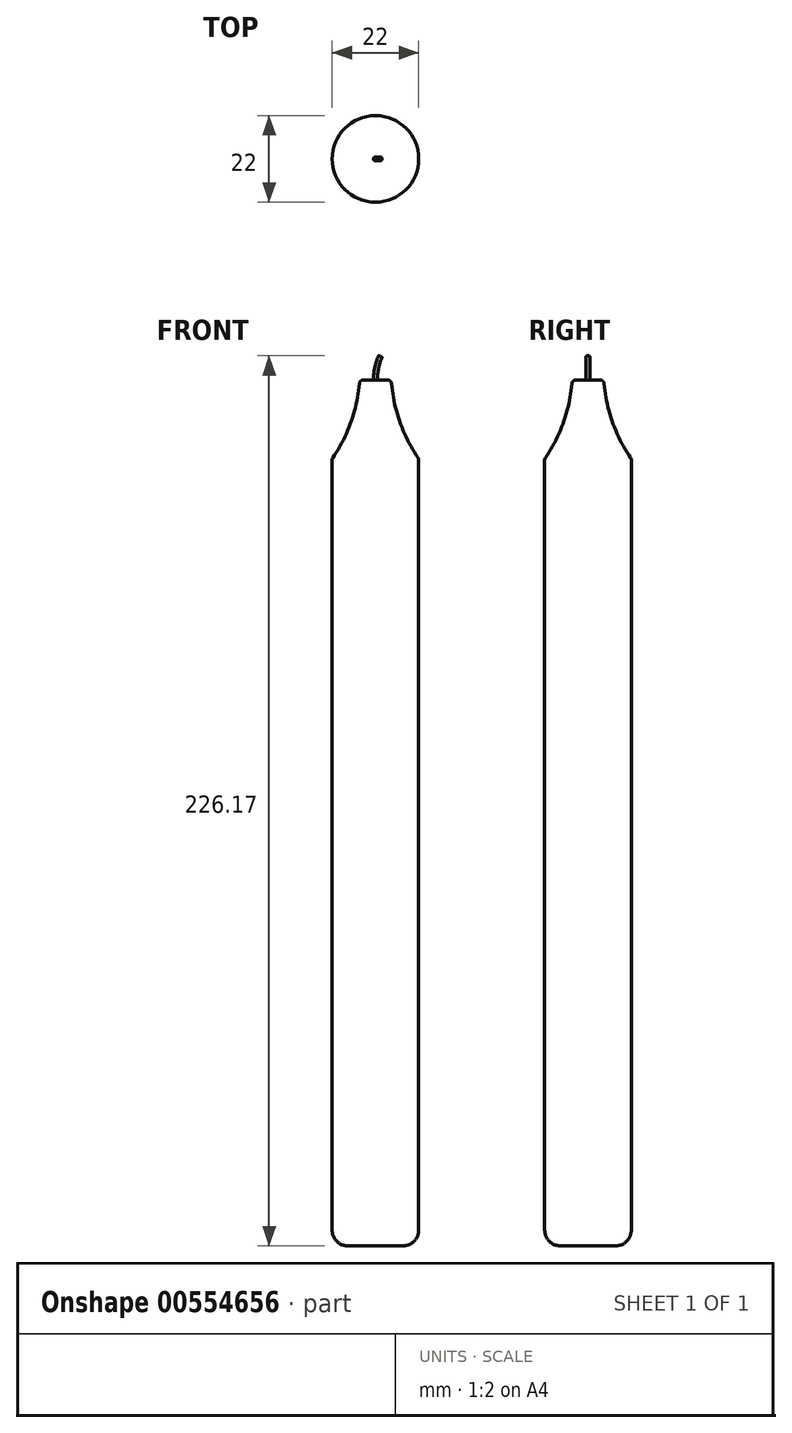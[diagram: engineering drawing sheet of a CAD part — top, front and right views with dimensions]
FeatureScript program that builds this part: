
annotation { "Feature Type Name" : "Feature", "Feature Type Description" : "" }
export const myFeature = defineFeature(function(context is Context, id is Id, definition is map)
    precondition{}
    {
        {
            var Q0;
            Q0=qCreatedBy(makeId("Front.planeOp"),FACE);
            var sketch = newSketch(context, id + "F0", { "sketchPlane" : qUnion([Q0])});
            skLineSegment(sketch, "E0", {"start": v(0, 0) * mm, "end": v(11, 0) * mm});
            skLineSegment(sketch, "E1", {"start": v(11, 0) * mm, "end": v(11, 200) * mm});
            skLineSegment(sketch, "E2", {"start": v(4, 220) * mm, "end": v(0, 220) * mm});
            skLineSegment(sketch, "E3", {"start": v(0, 220) * mm, "end": v(0, 0) * mm});
            skArc(sketch, "E4", {"start": v(4, 220) * mm, "mid": v(6.15, 209.53) * mm, "end": v(11, 200) * mm});
            skSolve(sketch);
        }
        {
            var Q0;
            Q0=makeQuery(id+"F0.imprint","IMPRINT",FACE,{"disambiguationData":[TD([[makeQuery(id+"F0.imprint","IMPRINT",EDGE,{"derivedFrom":sQuery(id+"F0.wireOp",EDGE,"E0")}),1.0]])]});
            var Q1;
            Q1=sQuery(id+"F0.wireOp",EDGE,"E3");
            revolve(context, id + "F1", {"entities" : qUnion([Q0]), "axis" : qUnion([Q1]), "revolveType" : RevolveType.FULL});
        }
        {
            var Q0;
            Q0=qCreatedBy(makeId("Front.planeOp"),FACE);
            var sketch = newSketch(context, id + "F2", { "sketchPlane" : qUnion([Q0])});
            skArc(sketch, "E5", {"start": v(1.25, 226) * mm, "mid": v(0.32, 223.06) * mm, "end": v(0, 220) * mm});
            skLineSegment(sketch, "E6", {"start": v(0, 220) * mm, "end": v(0, 0) * mm, "construction": true});
            skSolve(sketch);
        }
        {
            var Q0;
            Q0=makeQuery(id+"F1.opRevolve","SWEPT_FACE",FACE,{"disambiguationData":[OSD([sQuery(id+"F0.wireOp",EDGE,"E2")])]});
            var sketch = newSketch(context, id + "F3", { "sketchPlane" : qUnion([Q0])});
            skCircle(sketch, "E7", {"center": v(0, 0) * mm, "radius": 0.5 * mm});
            skSolve(sketch);
        }
        {
            var Q0;
            Q0=makeQuery(id+"F3.imprint","IMPRINT",FACE,{"disambiguationData":[TD([[makeQuery(id+"F3.imprint","IMPRINT",EDGE,{"derivedFrom":sQuery(id+"F3.wireOp",EDGE,"E7")}),1.0]])]});
            var Q1;
            Q1=sQuery(id+"F3.wireOp",EDGE,"E7");
            var Q2;
            Q2=sQuery(id+"F2.wireOp",EDGE,"E5");
            sweep(context, id + "F4", {"profiles" : qUnion([Q0]), "surfaceProfiles" : qUnion([Q1]), "path" : qUnion([Q2])});
        }
        {
            var Q0;
            Q0=makeQuery(id+"F1.opRevolve","SWEPT_EDGE",EDGE,{"disambiguationData":[OSD([sQuery(id+"F0.wireOp",EDGE,"E2"),sQuery(id+"F0.wireOp",EDGE,"E4")])]});
            var Q1;
            Q1=makeQuery(id+"F1.opRevolve","SWEPT_EDGE",EDGE,{"disambiguationData":[OSD([sQuery(id+"F0.wireOp",EDGE,"E1"),sQuery(id+"F0.wireOp",EDGE,"E4")])]});
            fillet(context, id + "F5", {"entities" : qUnion([Q0, Q1]), "radius" : 1 * mm, "tangentPropagation" : true, "allowEdgeOverflow" : false});
        }
        {
            var Q0;
            Q0=makeQuery(id+"F4.opSweep","CAP_EDGE",EDGE,{"disambiguationData":[OSD([sQuery(id+"F2.wireOp",VERTEX,"E5.start"),sQuery(id+"F3.wireOp",EDGE,"E7")])],"isStart":false});
            fillet(context, id + "F6", {"entities" : qUnion([Q0]), "radius" : 0.1 * mm, "tangentPropagation" : true, "allowEdgeOverflow" : false});
        }
        {
            var Q0;
            Q0=makeQuery(id+"F1.opRevolve","SWEPT_EDGE",EDGE,{"disambiguationData":[OSD([sQuery(id+"F0.wireOp",EDGE,"E0"),sQuery(id+"F0.wireOp",EDGE,"E1")])]});
            fillet(context, id + "F7", {"entities" : qUnion([Q0]), "radius" : 4 * mm, "tangentPropagation" : true, "allowEdgeOverflow" : false});
        }
    });
